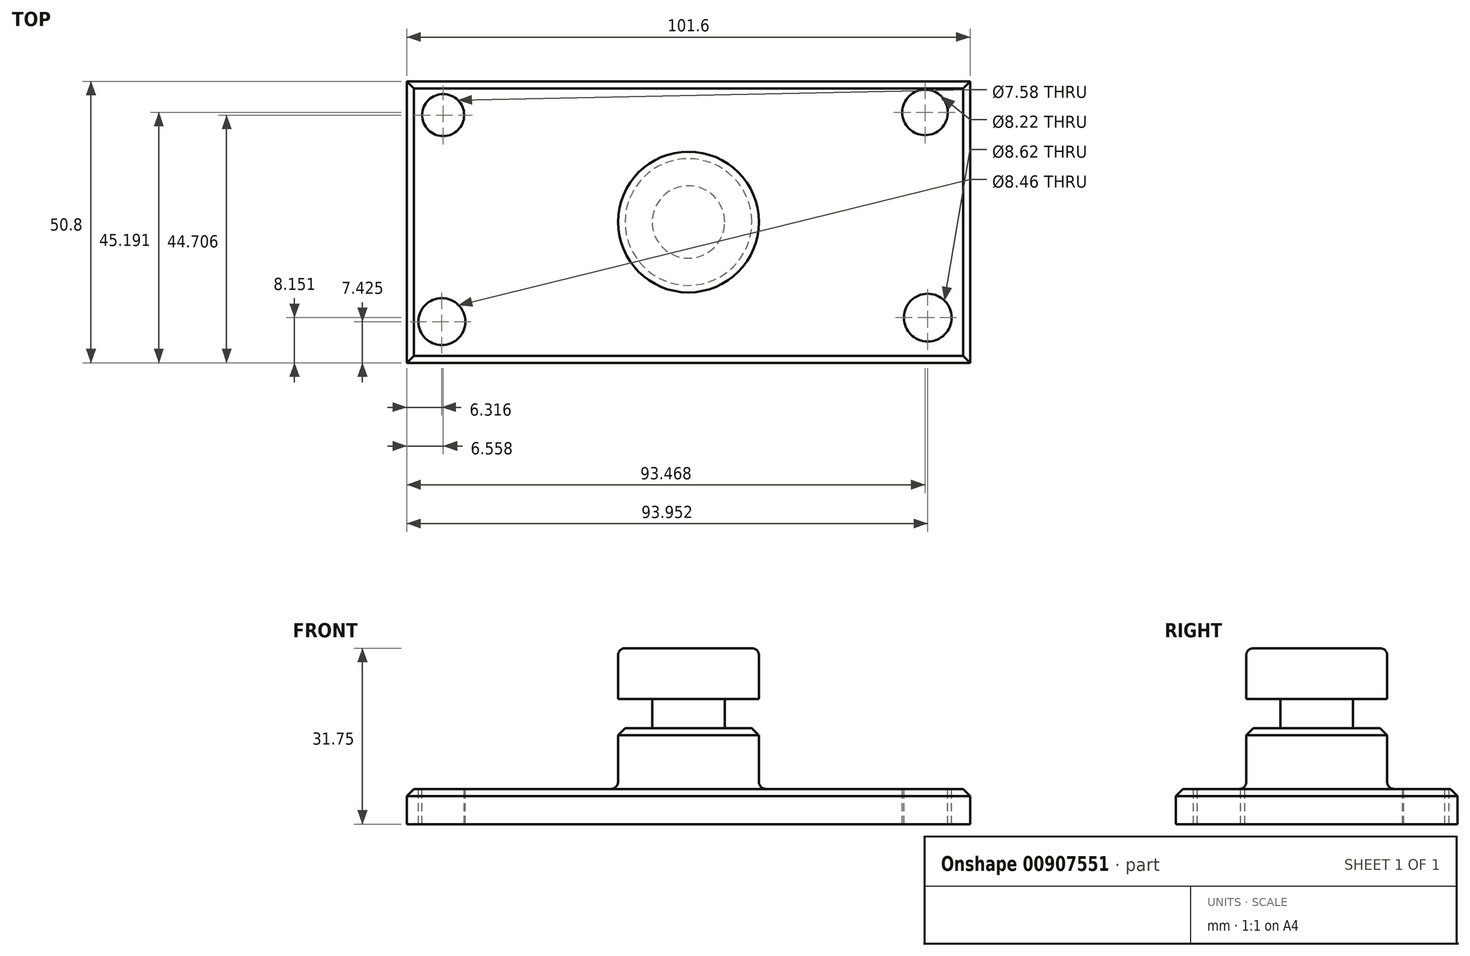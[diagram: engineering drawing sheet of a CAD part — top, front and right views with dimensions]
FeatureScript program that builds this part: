
annotation { "Feature Type Name" : "Feature", "Feature Type Description" : "" }
export const myFeature = defineFeature(function(context is Context, id is Id, definition is map)
    precondition{}
    {
        {
            var Q0;
            Q0=qCreatedBy(makeId("Top.planeOp"),FACE);
            var sketch = newSketch(context, id + "F0", { "sketchPlane" : qUnion([Q0])});
            skLineSegment(sketch, "E0.bottom", {"start": v(-50.8, 25.4) * mm, "end": v(50.8, 25.4) * mm});
            skLineSegment(sketch, "E0.top", {"start": v(-50.8, -25.4) * mm, "end": v(50.8, -25.4) * mm});
            skLineSegment(sketch, "E0.left", {"start": v(-50.8, 25.4) * mm, "end": v(-50.8, -25.4) * mm});
            skLineSegment(sketch, "E0.right", {"start": v(50.8, 25.4) * mm, "end": v(50.8, -25.4) * mm});
            skPoint(sketch, "E0.middle", {"position": v(0, 0) * mm});
            skSolve(sketch);
        }
        {
            var Q0;
            Q0=makeQuery(id+"F0.imprint","IMPRINT",FACE,{"disambiguationData":[TD([[makeQuery(id+"F0.imprint","IMPRINT",EDGE,{"derivedFrom":sQuery(id+"F0.wireOp",EDGE,"E0.bottom")}),-1.0]])]});
            extrude(context, id + "F1", {"entities" : qUnion([Q0]), "depth" : 6.35 * mm, "offsetDistance" : 25.4 * mm});
        }
        {
            var Q0;
            Q0=makeQuery(id+"F1.opExtrude","CAP_FACE",FACE,{"disambiguationData":[OSD([sQuery(id+"F0.wireOp",EDGE,"E0.bottom"),sQuery(id+"F0.wireOp",EDGE,"E0.top"),sQuery(id+"F0.wireOp",EDGE,"E0.left"),sQuery(id+"F0.wireOp",EDGE,"E0.right")])],"isStart":false});
            var sketch = newSketch(context, id + "F2", { "sketchPlane" : qUnion([Q0])});
            skCircle(sketch, "E1", {"center": v(-44.24, 19.3) * mm, "radius": 3.79 * mm});
            skCircle(sketch, "E2", {"center": v(-44.48, -17.98) * mm, "radius": 4.23 * mm});
            skCircle(sketch, "E3", {"center": v(42.67, 19.8) * mm, "radius": 4.1 * mm});
            skCircle(sketch, "E4", {"center": v(43.15, -17.25) * mm, "radius": 4.31 * mm});
            skSolve(sketch);
        }
        {
            var Q0;
            Q0=makeQuery(id+"F2.imprint","IMPRINT",FACE,{"disambiguationData":[TD([[makeQuery(id+"F2.imprint","IMPRINT",EDGE,{"derivedFrom":sQuery(id+"F2.wireOp",EDGE,"E1")}),1.0]])]});
            var Q1;
            Q1=makeQuery(id+"F2.imprint","IMPRINT",FACE,{"disambiguationData":[TD([[makeQuery(id+"F2.imprint","IMPRINT",EDGE,{"derivedFrom":sQuery(id+"F2.wireOp",EDGE,"E3")}),1.0]])]});
            var Q2;
            Q2=makeQuery(id+"F2.imprint","IMPRINT",FACE,{"disambiguationData":[TD([[makeQuery(id+"F2.imprint","IMPRINT",EDGE,{"derivedFrom":sQuery(id+"F2.wireOp",EDGE,"E4")}),1.0]])]});
            var Q3;
            Q3=makeQuery(id+"F2.imprint","IMPRINT",FACE,{"disambiguationData":[TD([[makeQuery(id+"F2.imprint","IMPRINT",EDGE,{"derivedFrom":sQuery(id+"F2.wireOp",EDGE,"E2")}),1.0]])]});
            extrude(context, id + "F3", {"entities" : qUnion([Q0, Q1, Q2, Q3]), "operationType" : NewBodyOperationType.REMOVE, "oppositeDirection" : true, "depth" : 6.35 * mm, "offsetDistance" : 25.4 * mm});
        }
        {
            var Q0;
            Q0=qCreatedBy(makeId("Front.planeOp"),FACE);
            var sketch = newSketch(context, id + "F4", { "sketchPlane" : qUnion([Q0])});
            skLineSegment(sketch, "E5.bottom", {"start": v(0, 0) * mm, "end": v(-12.7, 0) * mm});
            skLineSegment(sketch, "E5.top", {"start": v(0, 31.75) * mm, "end": v(-12.7, 31.75) * mm});
            skLineSegment(sketch, "E5.left", {"start": v(0, 0) * mm, "end": v(0, 31.75) * mm});
            skLineSegment(sketch, "E5.right", {"start": v(-12.7, 0) * mm, "end": v(-12.7, 31.75) * mm});
            skSolve(sketch);
        }
        {
            var Q0;
            Q0=makeQuery(id+"F4.imprint","IMPRINT",FACE,{"disambiguationData":[TD([[makeQuery(id+"F4.imprint","IMPRINT",EDGE,{"derivedFrom":sQuery(id+"F4.wireOp",EDGE,"E5.bottom")}),-1.0]])]});
            var Q1;
            Q1=sQuery(id+"F4.wireOp",EDGE,"E5.left");
            revolve(context, id + "F5", {"operationType" : NewBodyOperationType.ADD, "surfaceOperationType" : NewSurfaceOperationType.NEW, "entities" : qUnion([Q0]), "axis" : qUnion([Q1]), "revolveType" : RevolveType.FULL});
        }
        {
            var Q0;
            Q0=qCreatedBy(makeId("Front.planeOp"),FACE);
            var sketch = newSketch(context, id + "F6", { "sketchPlane" : qUnion([Q0])});
            skLineSegment(sketch, "E6.bottom", {"start": v(12.88, 22.58) * mm, "end": v(6.53, 22.58) * mm});
            skLineSegment(sketch, "E6.top", {"start": v(12.88, 17.29) * mm, "end": v(6.53, 17.29) * mm});
            skLineSegment(sketch, "E6.left", {"start": v(12.88, 22.58) * mm, "end": v(12.88, 17.29) * mm});
            skLineSegment(sketch, "E6.right", {"start": v(6.53, 22.58) * mm, "end": v(6.53, 17.29) * mm});
            skSolve(sketch);
        }
        {
            var Q0;
            Q0 = qSketchRegion(id + "F6", true);
            var Q1;
            Q1=makeQuery(id+"F5.opRevolve","SWEPT_FACE",FACE,{"disambiguationData":[OSD([sQuery(id+"F4.wireOp",EDGE,"E5.right")])]});
            revolve(context, id + "F7", {"operationType" : NewBodyOperationType.REMOVE, "surfaceOperationType" : NewSurfaceOperationType.NEW, "entities" : qUnion([Q0]), "axis" : qUnion([Q1]), "revolveType" : RevolveType.FULL, "oppositeDirection" : true});
        }
        {
            var Q0;
            Q0=makeQuery(id+"F1.opExtrude","CAP_EDGE",EDGE,{"disambiguationData":[OSD([sQuery(id+"F0.wireOp",EDGE,"E0.top")])],"isStart":false});
            var Q1;
            Q1=makeQuery(id+"F1.opExtrude","CAP_EDGE",EDGE,{"disambiguationData":[OSD([sQuery(id+"F0.wireOp",EDGE,"E0.left")])],"isStart":false});
            var Q2;
            Q2=makeQuery(id+"F1.opExtrude","CAP_EDGE",EDGE,{"disambiguationData":[OSD([sQuery(id+"F0.wireOp",EDGE,"E0.bottom")])],"isStart":false});
            var Q3;
            Q3=makeQuery(id+"F1.opExtrude","CAP_EDGE",EDGE,{"disambiguationData":[OSD([sQuery(id+"F0.wireOp",EDGE,"E0.right")])],"isStart":false});
            chamfer(context, id + "F8", {"entities" : qUnion([Q0, Q1, Q2, Q3]), "width" : 1.27 * mm, "tangentPropagation" : true});
        }
        {
            var Q0;
            Q0=makeQuery(id+"F5.boolean.opBoolean","INTERSECT",EDGE,{"derivedFrom":[makeQuery(id+"F1.opExtrude","CAP_FACE",FACE,{"disambiguationData":[OSD([sQuery(id+"F0.wireOp",EDGE,"E0.bottom"),sQuery(id+"F0.wireOp",EDGE,"E0.top"),sQuery(id+"F0.wireOp",EDGE,"E0.left"),sQuery(id+"F0.wireOp",EDGE,"E0.right")])],"isStart":false}),makeQuery(id+"F5.opRevolve","SWEPT_FACE",FACE,{"disambiguationData":[OSD([sQuery(id+"F4.wireOp",EDGE,"E5.right")])]})]});
            var Q1;
            Q1=makeQuery(id+"F5.opRevolve","SWEPT_EDGE",EDGE,{"disambiguationData":[OSD([sQuery(id+"F4.wireOp",EDGE,"E5.top"),sQuery(id+"F4.wireOp",EDGE,"E5.right")])]});
            fillet(context, id + "F9", {"entities" : qUnion([Q0, Q1]), "radius" : 1.27 * mm, "tangentPropagation" : true, "allowEdgeOverflow" : false});
        }
        {
            var Q0;
            Q0=makeQuery(id+"F7.boolean.opBoolean","INTERSECT",EDGE,{"derivedFrom":[makeQuery(id+"F5.opRevolve","SWEPT_FACE",FACE,{"disambiguationData":[OSD([sQuery(id+"F4.wireOp",EDGE,"E5.right")])]}),makeQuery(id+"F7.opRevolve","SWEPT_FACE",FACE,{"disambiguationData":[OSD([sQuery(id+"F6.wireOp",EDGE,"E6.top")])]})]});
            chamfer(context, id + "F10", {"entities" : qUnion([Q0]), "width" : 1.27 * mm, "tangentPropagation" : true});
        }
    });
